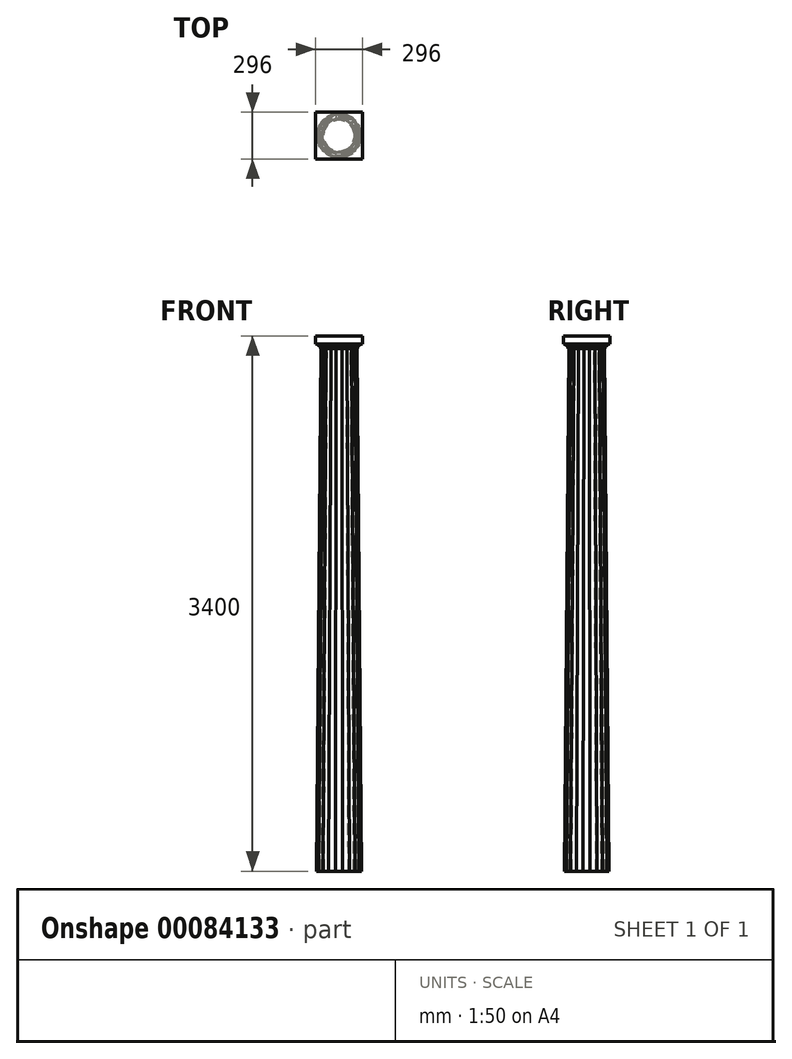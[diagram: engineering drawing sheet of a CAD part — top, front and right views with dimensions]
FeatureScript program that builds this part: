
annotation { "Feature Type Name" : "Feature", "Feature Type Description" : "" }
export const myFeature = defineFeature(function(context is Context, id is Id, definition is map)
    precondition{}
    {
        {
            assignVariable(context, id + "F0", {"name" : "H", "anyValue" : 3320});
        }
        {
            assignVariable(context, id + "F1", {"name" : "DO", "anyValue" : 196});
        }
        {
            var Q0;
            Q0=qCreatedBy(makeId("Top.planeOp"),FACE);
            var sketch = newSketch(context, id + "F2", { "sketchPlane" : qUnion([Q0])});
            skCircle(sketch, "E0", {"center": v(0, 0) * mm, "radius": 125 * mm});
            skLineSegment(sketch, "E1", {"start": v(0, 0) * mm, "end": v(0, -347.37) * mm, "construction": true});
            skLineSegment(sketch, "E2", {"start": v(0, 0) * mm, "end": v(-22.55, -142.37) * mm, "construction": true});
            skLineSegment(sketch, "E3.MirrorCS", {"start": v(0, 0) * mm, "end": v(22.55, -142.37) * mm, "construction": true});
            skLineSegment(sketch, "E4", {"start": v(-20.59, -130) * mm, "end": v(20.59, -130) * mm});
            skArc(sketch, "E5", {"start": v(22.55, -142.37) * mm, "mid": v(0, -137) * mm, "end": v(-22.55, -142.37) * mm});
            skPoint(sketch, "E6.orphan", {"position": v(-43.18, -272.6) * mm});
            skPoint(sketch, "E7.orphan", {"position": v(43.18, -272.6) * mm});
            skLineSegment(sketch, "E8", {"start": v(-22.55, -142.37) * mm, "end": v(-20.59, -130) * mm});
            skLineSegment(sketch, "E9", {"start": v(20.59, -130) * mm, "end": v(22.55, -142.37) * mm});
            skSolve(sketch);
        }
        {
            var Q0;
            Q0=qCreatedBy(makeId("Top.planeOp"),FACE);
            cPlane(context, id + "F3", {"entities" : qUnion([Q0]), "cplaneType" : CPlaneType.OFFSET, "offset" : (getVariable(context, 'H')) * mm, "width" : 150 * mm, "height" : 150 * mm});
        }
        {
            var Q0;
            Q0=qCreatedBy(id+"F3.planeOp",FACE);
            var sketch = newSketch(context, id + "F4", { "sketchPlane" : qUnion([Q0])});
            skCircle(sketch, "E10", {"center": v(0, 0) * mm, "radius": 98 * mm});
            skLineSegment(sketch, "E11", {"start": v(0, 0) * mm, "end": v(0, -205.56) * mm, "construction": true});
            skLineSegment(sketch, "E12", {"start": v(0, 0) * mm, "end": v(-17.95, -113.33) * mm, "construction": true});
            skLineSegment(sketch, "E13.MirrorCS", {"start": v(0, 0) * mm, "end": v(17.95, -113.33) * mm, "construction": true});
            skLineSegment(sketch, "E14", {"start": v(-16.31, -103) * mm, "end": v(16.31, -103) * mm});
            skArc(sketch, "E15", {"start": v(17.95, -113.33) * mm, "mid": v(0, -110) * mm, "end": v(-17.95, -113.33) * mm});
            skPoint(sketch, "E16.orphan", {"position": v(-43.18, -272.6) * mm});
            skPoint(sketch, "E17.orphan", {"position": v(43.18, -272.6) * mm});
            skLineSegment(sketch, "E18", {"start": v(-16.31, -103) * mm, "end": v(-17.95, -113.33) * mm});
            skLineSegment(sketch, "E19", {"start": v(16.31, -103) * mm, "end": v(17.95, -113.33) * mm});
            skSolve(sketch);
        }
        {
            var Q0;
            Q0=qCreatedBy(makeId("Front.planeOp"),FACE);
            var sketch = newSketch(context, id + "F5", { "sketchPlane" : qUnion([Q0])});
            skLineSegment(sketch, "E20", {"start": v(0, 0) * mm, "end": v(0, 3320) * mm});
            skLineSegment(sketch, "E21", {"start": v(0, 3320) * mm, "end": v(118, 3320) * mm});
            skLineSegment(sketch, "E22", {"start": v(143.17, 3350) * mm, "end": v(0, 3350) * mm});
            skLineSegment(sketch, "E23", {"start": v(0, 3350) * mm, "end": v(0, 3320) * mm});
            skLineSegment(sketch, "E24.bottom", {"start": v(0, 3350) * mm, "end": v(148, 3350) * mm});
            skLineSegment(sketch, "E24.top", {"start": v(0, 3400) * mm, "end": v(148, 3400) * mm});
            skLineSegment(sketch, "E24.left", {"start": v(0, 3350) * mm, "end": v(0, 3400) * mm});
            skLineSegment(sketch, "E24.right", {"start": v(148, 3350) * mm, "end": v(148, 3400) * mm});
            skLineSegment(sketch, "E25", {"start": v(118, 3320) * mm, "end": v(118, 3330) * mm});
            skLineSegment(sketch, "E26", {"start": v(118, 3330) * mm, "end": v(141.84, 3350) * mm});
            skSolve(sketch);
        }
        {
            var Q0;
            {var subQ2=sQuery(id+"F2.wireOp",EDGE,"E4");Q0=makeQuery(id+"F2.imprint","IMPRINT",FACE,{"disambiguationData":[TD([[makeQuery(id+"F2.imprint","IMPRINT",EDGE,{"derivedFrom":subQ2}),-1.0]])]});}
            var Q1;
            {var subQ2=sQuery(id+"F4.wireOp",EDGE,"E14");Q1=makeQuery(id+"F4.imprint","IMPRINT",FACE,{"disambiguationData":[TD([[makeQuery(id+"F4.imprint","IMPRINT",EDGE,{"derivedFrom":subQ2}),-1.0]])]});}
            loft(context, id + "F6", {"sheetProfilesArray" : [{ "sheetProfileEntities" : qUnion([Q0]) }, { "sheetProfileEntities" : qUnion([Q1]) }]});
        }
        {
            var Q0;
            {var subQ2=sQuery(id+"F4.wireOp",EDGE,"E14");var subQ6=sQuery(id+"F2.wireOp",EDGE,"E4");Q0=makeQuery(id+"F6.opLoft","SWEPT_BODY",BODY,{"disambiguationData":[OSD([makeQuery(id+"F2.imprint","IMPRINT",FACE,{"disambiguationData":[TD([[makeQuery(id+"F2.imprint","IMPRINT",EDGE,{"derivedFrom":subQ6}),-1.0]])]}),makeQuery(id+"F4.imprint","IMPRINT",FACE,{"disambiguationData":[TD([[makeQuery(id+"F4.imprint","IMPRINT",EDGE,{"derivedFrom":subQ2}),-1.0]])]})])]});}
            var Q1;
            Q1=sQuery(id+"F5.wireOp",EDGE,"E20");
            circularPattern(context, id + "F7", {"entities" : qUnion([Q0]), "axis" : qUnion([Q1]), "angle" : 18 * degree, "instanceCount" : 20, "computeTransformsWithoutBuiltin" : true});
        }
        {
            var Q0;
            Q0=makeQuery(id+"F5.imprint","IMPRINT",FACE,{"disambiguationData":[TD([[makeQuery(id+"F5.imprint","IMPRINT",EDGE,{"derivedFrom":sQuery(id+"F5.wireOp",EDGE,"E21")}),1.0]])]});
            var Q1;
            Q1=sQuery(id+"F5.wireOp",EDGE,"E23");
            revolve(context, id + "F8", {"entities" : qUnion([Q0]), "axis" : qUnion([Q1]), "revolveType" : RevolveType.FULL});
        }
        {
            var Q0;
            Q0=makeQuery(id+"F5.imprint","IMPRINT",FACE,{"disambiguationData":[TD([[makeQuery(id+"F5.imprint","IMPRINT",EDGE,{"derivedFrom":sQuery(id+"F5.wireOp",EDGE,"E24.top")}),-1.0]])]});
            extrude(context, id + "F9", {"entities" : qUnion([Q0]), "depth" : ((getVariable(context, 'DO')) + 30 + 30 + 20 + 20) * mm, "symmetric" : true});
        }
        {
            var Q0;
            Q0=makeQuery(id+"F9.opExtrude","SWEPT_BODY",BODY,{"disambiguationData":[OSD([sQuery(id+"F5.wireOp",EDGE,"E24.bottom"),sQuery(id+"F5.wireOp",EDGE,"E24.top"),sQuery(id+"F5.wireOp",EDGE,"E24.left"),sQuery(id+"F5.wireOp",EDGE,"E24.right")])]});
            var Q1;
            Q1=makeQuery(id+"F9.opExtrude","SWEPT_FACE",FACE,{"disambiguationData":[OSD([sQuery(id+"F5.wireOp",EDGE,"E24.left")])]});
            mirror(context, id + "F10", {"operationType" : NewBodyOperationType.ADD, "entities" : qUnion([Q0]), "mirrorPlane" : qUnion([Q1])});
        }
        {
            var Q0;
            Q0=makeQuery(id+"F2.imprint","IMPRINT",FACE,{"disambiguationData":[TD([[makeQuery(id+"F2.imprint","IMPRINT",EDGE,{"derivedFrom":sQuery(id+"F2.wireOp",EDGE,"E0")}),1.0]])]});
            var Q1;
            Q1=makeQuery(id+"F4.imprint","IMPRINT",FACE,{"disambiguationData":[TD([[makeQuery(id+"F4.imprint","IMPRINT",EDGE,{"derivedFrom":sQuery(id+"F4.wireOp",EDGE,"E10")}),1.0]])]});
            loft(context, id + "F11", {"sheetProfilesArray" : [{ "sheetProfileEntities" : qUnion([Q0]) }, { "sheetProfileEntities" : qUnion([Q1]) }]});
        }
    });
